# Revit family: BuzziCone Series
name_source: partatom
category: Lighting Fixtures
revit_build: Autodesk Revit 2018 (Build: 20190510_1515(x64)
units: mm (PartAtom-declared; Revit-internal decimal feet)

## family parameters
Always vertical = Yes
Cut with Voids When Loaded = No
Host = Ceiling
Light Source = Yes
OmniClass Number = 23.80.70.11
OmniClass Title = Luminaries for Internal Lighting
Part Type = Normal
Room Calculation Point = No
Round Connector Dimension = Use Diameter
Shared = No

## types (6) — shared parameters
Bulb = <By Category>
Canopy = <By Category>
Color Filter = 16777215
Dimming Lamp Color Temperature Shift = <None>
Housing = <By Category>
Inner Shade = <By Category>
Light Source Symbol Size = 2' - 0"
Outer Shade = <By Category>

## per-type parameters (varying)
| type | Light Source Type | Shade Type | bottom of shade |
| BuzziCone 47- LED Globe | Bulb | Shade 47 | 1' - 5 9/16" |
| BuzziCone 102-LED Globe | Bulb | Shade 102 | 0' - 7" |
| BuzziCone 133- LED Globe | Bulb | Shade 133 | 0' - 3 7/16" |
| BuzziCone 102-LED Spot | Bulb : Spot | Shade 102 | 0' - 7" |
| BuzziCone 133-LED Spot | Bulb : Spot | Shade 133 | 0' - 3 7/16" |
| BuzziCone 47-LED Spot | Bulb : Spot | Shade 47 | 1' - 5 9/16" |

## geometry (parser evidence)
native form markers: Sweep x15
no freeform markers — native parametric forms only
